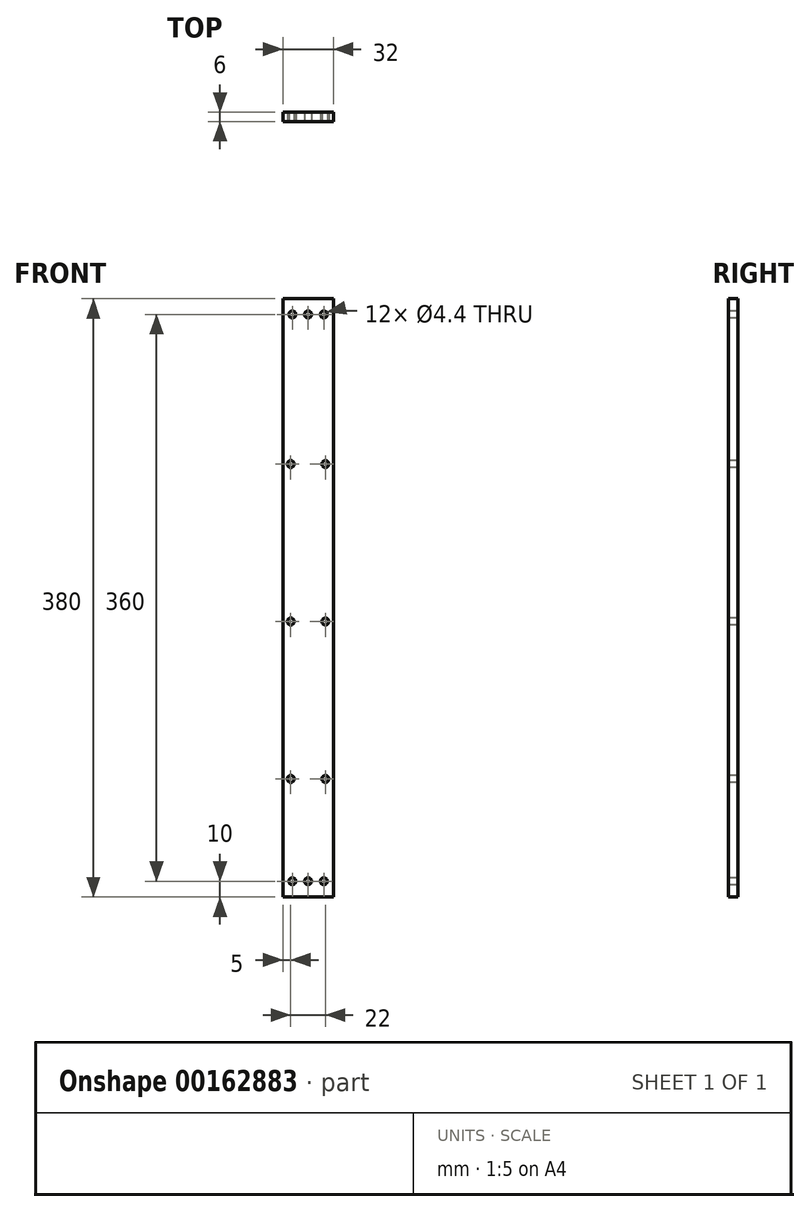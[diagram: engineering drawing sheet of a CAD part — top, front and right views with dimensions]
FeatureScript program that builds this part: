
annotation { "Feature Type Name" : "Feature", "Feature Type Description" : "" }
export const myFeature = defineFeature(function(context is Context, id is Id, definition is map)
    precondition{}
    {
        {
            var Q0;
            Q0=qCreatedBy(makeId("Front.planeOp"),FACE);
            var sketch = newSketch(context, id + "F0", { "sketchPlane" : qUnion([Q0])});
            skLineSegment(sketch, "E0.bottom", {"start": v(16, -190) * mm, "end": v(-16, -190) * mm});
            skLineSegment(sketch, "E0.top", {"start": v(16, 190) * mm, "end": v(-16, 190) * mm});
            skLineSegment(sketch, "E0.left", {"start": v(16, -190) * mm, "end": v(16, 190) * mm});
            skLineSegment(sketch, "E0.right", {"start": v(-16, -190) * mm, "end": v(-16, 190) * mm});
            skPoint(sketch, "E0.middle", {"position": v(0, 0) * mm});
            skLineSegment(sketch, "E1", {"start": v(-16, -180) * mm, "end": v(16, -180) * mm, "construction": true});
            skPoint(sketch, "E2", {"position": v(0, -180) * mm});
            skPoint(sketch, "E3", {"position": v(-10, -180) * mm});
            skPoint(sketch, "E4.MirrorP", {"position": v(10, -180) * mm});
            skPoint(sketch, "E5.MirrorP", {"position": v(-10, 180) * mm});
            skPoint(sketch, "E6.MirrorP", {"position": v(0, 180) * mm});
            skPoint(sketch, "E7.MirrorP", {"position": v(10, 180) * mm});
            skPoint(sketch, "E8", {"position": v(-11, -115) * mm});
            skPoint(sketch, "E9.0.1.0", {"position": v(-11, -15) * mm});
            skPoint(sketch, "E9.0.2.0", {"position": v(-11, 85) * mm});
            skLineSegment(sketch, "E9.direction1", {"start": v(-11, -115) * mm, "end": v(18.23, -115) * mm, "construction": true});
            skLineSegment(sketch, "E9.direction2", {"start": v(-11, -115) * mm, "end": v(-11, -15) * mm, "construction": true});
            skPoint(sketch, "E10.MirrorP", {"position": v(11, 85) * mm});
            skPoint(sketch, "E11.MirrorP", {"position": v(11, -15) * mm});
            skPoint(sketch, "E12.MirrorP", {"position": v(11, -115) * mm});
            skSolve(sketch);
        }
        {
            var Q0;
            Q0=makeQuery(id+"F0.imprint","IMPRINT",FACE,{"disambiguationData":[TD([[makeQuery(id+"F0.imprint","IMPRINT",EDGE,{"derivedFrom":sQuery(id+"F0.wireOp",EDGE,"E0.bottom")}),-1.0]])]});
            extrude(context, id + "F1", {"entities" : qUnion([Q0]), "oppositeDirection" : true, "depth" : 6 * mm});
        }
        {
            var Q0;
            Q0=sQuery(id+"F0.wireOp",VERTEX,"E3");
            var Q1;
            Q1=sQuery(id+"F0.wireOp",VERTEX,"E2");
            var Q2;
            Q2=sQuery(id+"F0.wireOp",VERTEX,"E4.MirrorP");
            var Q3;
            Q3=sQuery(id+"F0.wireOp",VERTEX,"E5.MirrorP");
            var Q4;
            Q4=sQuery(id+"F0.wireOp",VERTEX,"E6.MirrorP");
            var Q5;
            Q5=sQuery(id+"F0.wireOp",VERTEX,"E7.MirrorP");
            var Q6;
            Q6=sQuery(id+"F0.wireOp",VERTEX,"E8");
            var Q7;
            Q7=sQuery(id+"F0.wireOp",VERTEX,"E12.MirrorP");
            var Q8;
            Q8=sQuery(id+"F0.wireOp",VERTEX,"E9.0.1.0");
            var Q9;
            Q9=sQuery(id+"F0.wireOp",VERTEX,"E11.MirrorP");
            var Q10;
            Q10=sQuery(id+"F0.wireOp",VERTEX,"E9.0.2.0");
            var Q11;
            Q11=sQuery(id+"F0.wireOp",VERTEX,"E10.MirrorP");
            var Q12;
            Q12=makeQuery(id+"F1.opExtrude","SWEPT_BODY",BODY,{"disambiguationData":[OSD([sQuery(id+"F0.wireOp",EDGE,"E0.bottom"),sQuery(id+"F0.wireOp",EDGE,"E0.top"),sQuery(id+"F0.wireOp",EDGE,"E0.left"),sQuery(id+"F0.wireOp",EDGE,"E0.right")])]});
            hole(context, id + "F2", {"style" : HoleStyle.SIMPLE, "endStyle" : HoleEndStyle.BLIND, "standardTappedOrClearance" : lookupTablePath({ "standard" : "ISO", "fit" : "Normal", "size" : "M4", "type" : "Clearance" }), "standardBlindInLast" : lookupTablePath({ "fit" : "Standard", "standard" : "ISO", "size" : "M4", "type" : "Clearance" }), "holeDiameter" : 4.4 * mm, "holeDepth" : 10 * mm, "startFromSketch" : true, "locations" : qUnion([Q0, Q1, Q2, Q3, Q4, Q5, Q6, Q7, Q8, Q9, Q10, Q11]), "scope" : qUnion([Q12])});
        }
    });
